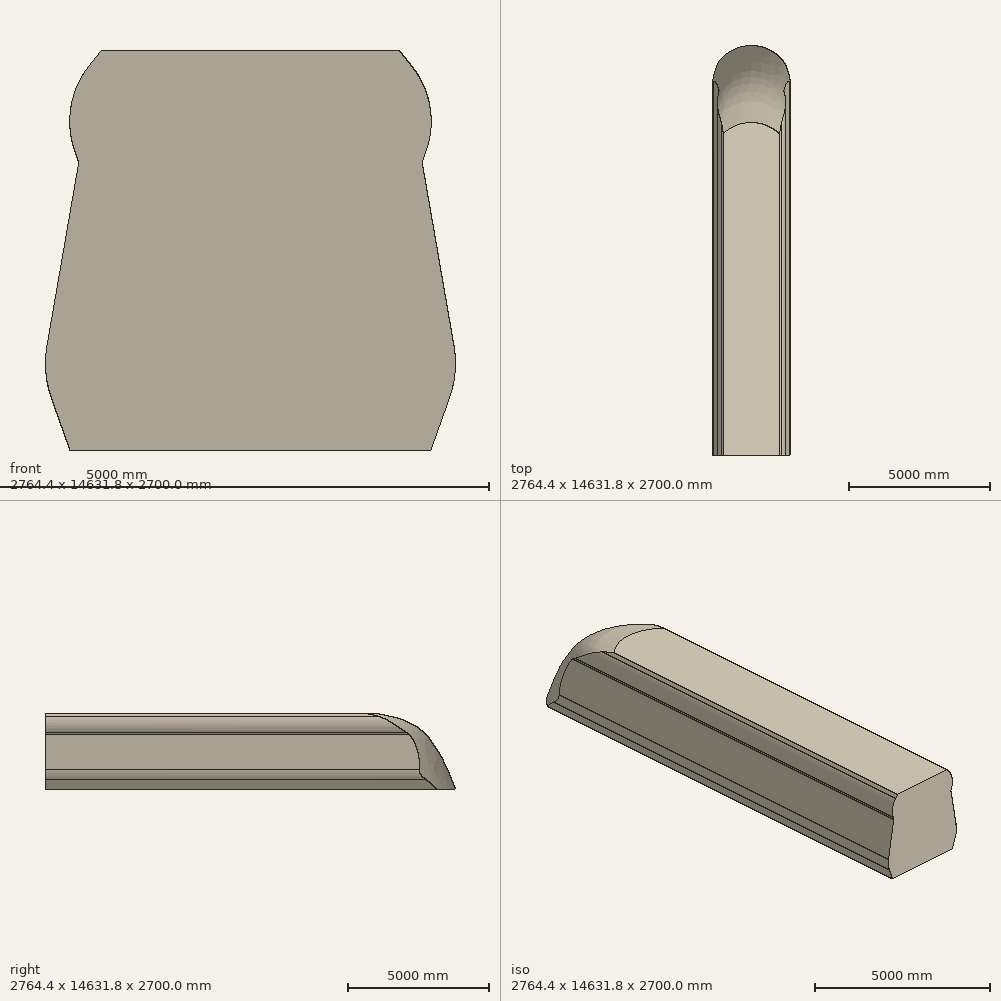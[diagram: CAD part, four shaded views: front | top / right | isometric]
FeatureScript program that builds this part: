
annotation { "Feature Type Name" : "Feature", "Feature Type Description" : "" }
export const myFeature = defineFeature(function(context is Context, id is Id, definition is map)
    precondition{}
    {
        {
            var Q0;
            Q0=qCreatedBy(makeId("Front.planeOp"),FACE);
            var sketch = newSketch(context, id + "F0", { "sketchPlane" : qUnion([Q0])});
            skLineSegment(sketch, "E0.bottom", {"start": v(1215.39, -1350) * mm, "end": v(-1215.39, -1350) * mm});
            skLineSegment(sketch, "E0.top", {"start": v(1001.2, 1350) * mm, "end": v(-1001.2, 1350) * mm});
            skPoint(sketch, "E0.middle", {"position": v(0, 0) * mm});
            skLineSegment(sketch, "E1", {"start": v(-1403.5, -825.57) * mm, "end": v(-1157.21, 592.63) * mm});
            skLineSegment(sketch, "E2", {"start": v(-1157.21, 592.63) * mm, "end": v(-1298.03, 984.46) * mm});
            skLineSegment(sketch, "E3", {"start": v(-1298.03, 984.46) * mm, "end": v(-1001.2, 1350) * mm});
            skPoint(sketch, "E4.orphan", {"position": v(-1494.59, 1350) * mm});
            skLineSegment(sketch, "E5.MirrorCS", {"start": v(1298.03, 984.46) * mm, "end": v(1001.2, 1350) * mm});
            skLineSegment(sketch, "E6.MirrorCS", {"start": v(1157.21, 592.63) * mm, "end": v(1298.03, 984.46) * mm});
            skLineSegment(sketch, "E7.MirrorCS", {"start": v(1403.5, -825.57) * mm, "end": v(1157.21, 592.63) * mm});
            skPoint(sketch, "E0.left.end.orphan", {"position": v(1494.59, 1350) * mm});
            skLineSegment(sketch, "E8", {"start": v(1215.39, -1350) * mm, "end": v(1403.5, -825.57) * mm});
            skLineSegment(sketch, "E9.MirrorCS", {"start": v(-1215.39, -1350) * mm, "end": v(-1403.5, -825.57) * mm});
            skPoint(sketch, "E10.orphan", {"position": v(1494.59, -1350) * mm});
            skPoint(sketch, "E11.orphan", {"position": v(-1494.59, -1350) * mm});
            skSolve(sketch);
        }
        {
            var Q0;
            Q0=makeQuery(id+"F0.imprint","IMPRINT",FACE,{"disambiguationData":[TD([[makeQuery(id+"F0.imprint","IMPRINT",EDGE,{"derivedFrom":sQuery(id+"F0.wireOp",EDGE,"E0.bottom")}),-1.0]])]});
            extrude(context, id + "F1", {"entities" : qUnion([Q0]), "depth" : 14770 * mm, "offsetDistance" : 25 * mm});
        }
        {
            var Q0;
            Q0=qCreatedBy(makeId("Right.planeOp"),FACE);
            var sketch = newSketch(context, id + "F2", { "sketchPlane" : qUnion([Q0])});
            skFitSpline(sketch, "E12", {"points": [v(-3977.67, 1461.98) * mm, v(-1399.02, 824.1) * mm, v(0, -1605.26) * mm], "startDerivative": vector(5836.12, -429.7) * mm, "endDerivative": vector(2135.83, -5681.2) * mm});
            skPoint(sketch, "E13.start.orphan", {"position": v(772.48, -1605.26) * mm});
            skSolve(sketch);
        }
        {
            var Q0;
            Q0=makeQuery(id+"F1.opExtrude","SWEPT_EDGE",EDGE,{"disambiguationData":[OSD([sQuery(id+"F0.wireOp",EDGE,"E7.MirrorCS"),sQuery(id+"F0.wireOp",EDGE,"E8")])]});
            var Q1;
            Q1=makeQuery(id+"F1.opExtrude","SWEPT_EDGE",EDGE,{"disambiguationData":[OSD([sQuery(id+"F0.wireOp",EDGE,"E1"),sQuery(id+"F0.wireOp",EDGE,"E9.MirrorCS")])]});
            fillet(context, id + "F3", {"entities" : qUnion([Q0, Q1]), "radius" : 700 * mm, "tangentPropagation" : true, "allowEdgeOverflow" : false});
        }
        {
            var Q0;
            Q0=makeQuery(id+"F1.opExtrude","SWEPT_EDGE",EDGE,{"disambiguationData":[OSD([sQuery(id+"F0.wireOp",EDGE,"E5.MirrorCS"),sQuery(id+"F0.wireOp",EDGE,"E6.MirrorCS")])]});
            var Q1;
            Q1=makeQuery(id+"F1.opExtrude","SWEPT_EDGE",EDGE,{"disambiguationData":[OSD([sQuery(id+"F0.wireOp",EDGE,"E2"),sQuery(id+"F0.wireOp",EDGE,"E3")])]});
            fillet(context, id + "F4", {"entities" : qUnion([Q0, Q1]), "radius" : 600 * mm, "tangentPropagation" : true, "allowEdgeOverflow" : false});
        }
        {
            var Q0;
            Q0=makeQuery(id+"F1.opExtrude","SWEPT_FACE",FACE,{"disambiguationData":[OSD([sQuery(id+"F0.wireOp",EDGE,"E0.bottom")])]});
            var sketch = newSketch(context, id + "F5", { "sketchPlane" : qUnion([Q0])});
            skArc(sketch, "E14", {"start": v(-1437.68, 1575.9) * mm, "mid": v(0, 138.22) * mm, "end": v(1437.68, 1575.9) * mm});
            skLineSegment(sketch, "E15", {"start": v(1437.68, 1575.9) * mm, "end": v(2292.61, 1575.9) * mm});
            skLineSegment(sketch, "E16", {"start": v(2292.61, 1575.9) * mm, "end": v(2292.61, -4152.24) * mm});
            skLineSegment(sketch, "E17", {"start": v(-2569.65, -4152.24) * mm, "end": v(-2569.65, 1575.9) * mm});
            skLineSegment(sketch, "E18", {"start": v(-2569.65, 1575.9) * mm, "end": v(-1437.68, 1575.9) * mm});
            skLineSegment(sketch, "E19", {"start": v(-2569.65, -4152.24) * mm, "end": v(2292.61, -4152.24) * mm});
            skSolve(sketch);
        }
        {
            var Q0;
            {var subQ1=sQuery(id+"F0.wireOp",EDGE,"E0.bottom");var subQ6=makeQuery(id+"F1.opExtrude","CAP_EDGE",EDGE,{"disambiguationData":[OSD([subQ1])],"isStart":true});Q0=makeQuery(id+"F5.imprint","IMPRINT",FACE,{"disambiguationData":[TD([[makeQuery(id+"F5.imprint","IMPRINT",EDGE,{"derivedFrom":subQ6}),-1.0]])]});}
            var Q1;
            {var subQ0=sQuery(id+"F5.wireOp",EDGE,"E15");Q1=makeQuery(id+"F5.imprint","IMPRINT",FACE,{"disambiguationData":[TD([[makeQuery(id+"F5.imprint","IMPRINT",EDGE,{"derivedFrom":subQ0}),-1.0]])]});}
            var Q2;
            Q2=sQuery(id+"F2.wireOp",EDGE,"E12");
            sweep(context, id + "F6", {"operationType" : NewBodyOperationType.REMOVE, "profiles" : qUnion([Q0, Q1]), "path" : qUnion([Q2]), "keepProfileOrientation" : true});
        }
    });
